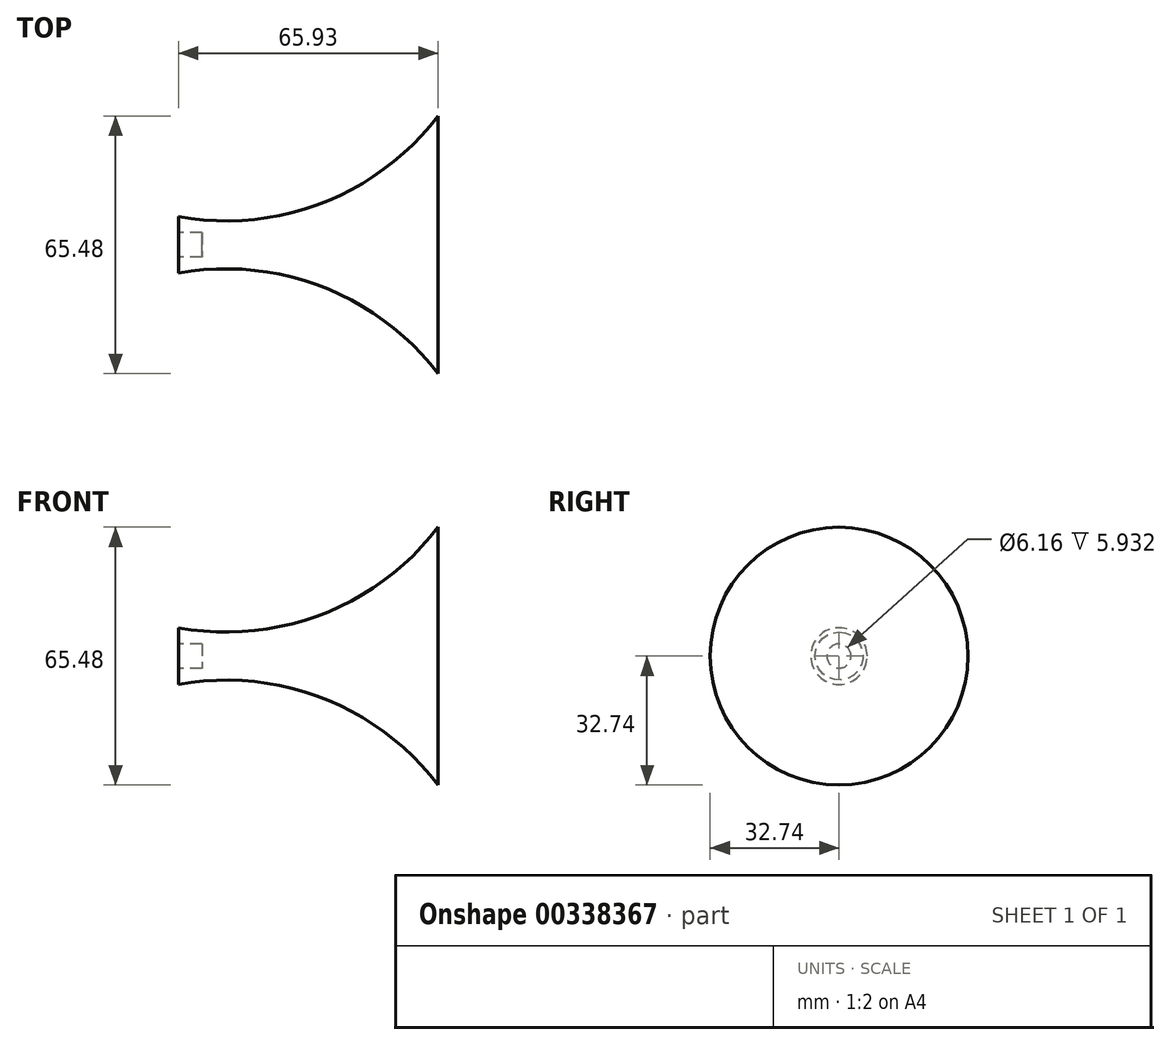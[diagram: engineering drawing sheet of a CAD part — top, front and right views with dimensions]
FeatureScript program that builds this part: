
annotation { "Feature Type Name" : "Feature", "Feature Type Description" : "" }
export const myFeature = defineFeature(function(context is Context, id is Id, definition is map)
    precondition{}
    {
        {
            var Q0;
            Q0=qCreatedBy(makeId("Top.planeOp"),FACE);
            var sketch = newSketch(context, id + "F0", { "sketchPlane" : qUnion([Q0])});
            skLineSegment(sketch, "E0", {"start": v(0, 0) * mm, "end": v(60, 0) * mm, "construction": true});
            skLineSegment(sketch, "E1", {"start": v(60, 0) * mm, "end": v(60, 32.74) * mm});
            skArc(sketch, "E2", {"start": v(-5.93, 7.19) * mm, "mid": v(30.64, 10.67) * mm, "end": v(60, 32.74) * mm});
            skLineSegment(sketch, "E3", {"start": v(-5.93, 7.19) * mm, "end": v(-5.93, 3.08) * mm});
            skLineSegment(sketch, "E4", {"start": v(-5.93, 3.08) * mm, "end": v(0, 3.08) * mm});
            skLineSegment(sketch, "E5", {"start": v(0, 3.08) * mm, "end": v(0, 0) * mm});
            skLineSegment(sketch, "E6", {"start": v(0, 0) * mm, "end": v(60, 0) * mm});
            skSolve(sketch);
        }
        {
            var Q0;
            Q0 = qSketchRegion(id + "F0", true);
            var Q1;
            Q1=sQuery(id+"F0.wireOp",EDGE,"E6");
            revolve(context, id + "F1", {"entities" : qUnion([Q0]), "axis" : qUnion([Q1]), "revolveType" : RevolveType.FULL});
        }
    });
